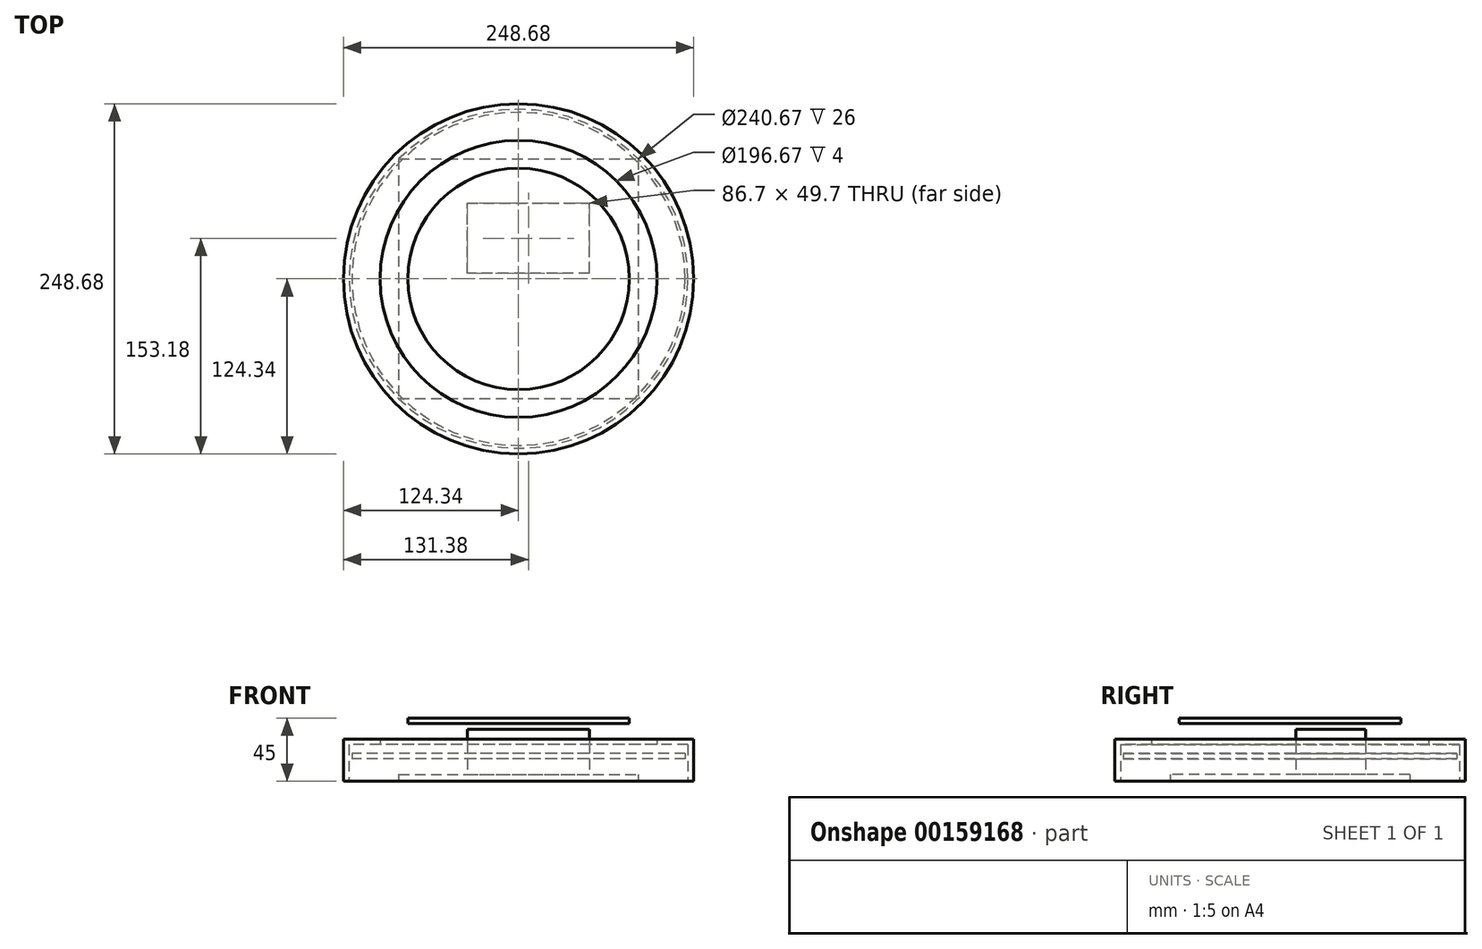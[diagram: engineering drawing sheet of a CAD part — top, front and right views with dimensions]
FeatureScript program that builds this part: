
annotation { "Feature Type Name" : "Feature", "Feature Type Description" : "" }
export const myFeature = defineFeature(function(context is Context, id is Id, definition is map)
    precondition{}
    {
        {
            var Q0;
            Q0=qCreatedBy(makeId("Top.planeOp"),FACE);
            var sketch = newSketch(context, id + "F0", { "sketchPlane" : qUnion([Q0])});
            skLineSegment(sketch, "E0.bottom", {"start": v(0, 0) * mm, "end": v(170.18, 0) * mm});
            skLineSegment(sketch, "E0.top", {"start": v(0, -170.18) * mm, "end": v(170.18, -170.18) * mm});
            skLineSegment(sketch, "E0.left", {"start": v(0, 0) * mm, "end": v(0, -170.18) * mm});
            skLineSegment(sketch, "E0.right", {"start": v(170.18, 0) * mm, "end": v(170.18, -170.18) * mm});
            skSolve(sketch);
        }
        {
            var Q0;
            Q0 = qSketchRegion(id + "F0", true);
            extrude(context, id + "F1", {"entities" : qUnion([Q0]), "depth" : 5 * mm});
        }
        {
            var Q0;
            Q0=makeQuery(id+"F1.opExtrude","CAP_FACE",FACE,{"disambiguationData":[OSD([sQuery(id+"F0.wireOp",EDGE,"E0.bottom"),sQuery(id+"F0.wireOp",EDGE,"E0.top"),sQuery(id+"F0.wireOp",EDGE,"E0.left"),sQuery(id+"F0.wireOp",EDGE,"E0.right")])],"isStart":true});
            var sketch = newSketch(context, id + "F2", { "sketchPlane" : qUnion([Q0])});
            skLineSegment(sketch, "E1.bottom", {"start": v(135.48, 81.1) * mm, "end": v(48.78, 81.1) * mm});
            skLineSegment(sketch, "E1.top", {"start": v(48.78, 31.4) * mm, "end": v(135.48, 31.4) * mm});
            skLineSegment(sketch, "E1.left", {"start": v(135.48, 81.1) * mm, "end": v(135.48, 31.4) * mm});
            skLineSegment(sketch, "E1.right", {"start": v(48.78, 81.1) * mm, "end": v(48.78, 31.4) * mm});
            skSolve(sketch);
        }
        {
            var Q0;
            Q0 = qSketchRegion(id + "F2", true);
            extrude(context, id + "F3", {"entities" : qUnion([Q0]), "operationType" : NewBodyOperationType.ADD, "oppositeDirection" : true, "depth" : 37 * mm});
        }
        {
            var Q0;
            Q0=qCreatedBy(makeId("Top.planeOp"),FACE);
            var sketch = newSketch(context, id + "F4", { "sketchPlane" : qUnion([Q0])});
            skCircle(sketch, "E2", {"center": v(85.1, -85.1) * mm, "radius": 120.34 * mm});
            skPoint(sketch, "E3", {"position": v(0, 0) * mm});
            skPoint(sketch, "E4", {"position": v(170.18, -170.18) * mm});
            skCircle(sketch, "E5", {"center": v(85.1, -85.1) * mm, "radius": 124.34 * mm});
            skSolve(sketch);
        }
        {
            var Q0;
            Q0=makeQuery(id+"F1.opExtrude","CAP_FACE",FACE,{"disambiguationData":[OSD([sQuery(id+"F0.wireOp",EDGE,"E0.bottom"),sQuery(id+"F0.wireOp",EDGE,"E0.top"),sQuery(id+"F0.wireOp",EDGE,"E0.left"),sQuery(id+"F0.wireOp",EDGE,"E0.right")])],"isStart":false});
            var sketch = newSketch(context, id + "F5", { "sketchPlane" : qUnion([Q0])});
            skCircle(sketch, "E6", {"center": v(85.1, -85.1) * mm, "radius": 118.34 * mm});
            skSolve(sketch);
        }
        {
            var Q0;
            Q0 = qSketchRegion(id + "F5", true);
            extrude(context, id + "F6", {"entities" : qUnion([Q0]), "operationType" : NewBodyOperationType.ADD, "depth" : (.4 * 37) * mm, "hasSecondDirection" : true, "secondDirectionOppositeDirection" : false, "secondDirectionDepth" : 11 * mm});
        }
        {
            var Q0;
            Q0=makeQuery(id+"F6.opExtrude","CAP_FACE",FACE,{"disambiguationData":[OSD([sQuery(id+"F5.wireOp",EDGE,"E6")])],"isStart":false});
            var sketch = newSketch(context, id + "F7", { "sketchPlane" : qUnion([Q0])});
            skCircle(sketch, "E7", {"center": v(85.1, -85.1) * mm, "radius": 108.34 * mm});
            skSolve(sketch);
        }
        {
            var Q0;
            Q0=makeQuery(id+"F4.imprint","IMPRINT",FACE,{"disambiguationData":[TD([[makeQuery(id+"F4.imprint","IMPRINT",EDGE,{"derivedFrom":sQuery(id+"F4.wireOp",EDGE,"E2")}),-1.0]])]});
            extrude(context, id + "F8", {"entities" : qUnion([Q0]), "depth" : 26 * mm});
        }
        {
            var Q0;
            Q0=makeQuery(id+"F8.opExtrude","CAP_FACE",FACE,{"disambiguationData":[OSD([sQuery(id+"F4.wireOp",EDGE,"E2"),sQuery(id+"F4.wireOp",EDGE,"E5")])],"isStart":false});
            var sketch = newSketch(context, id + "F9", { "sketchPlane" : qUnion([Q0])});
            skCircle(sketch, "E8", {"center": v(85.1, -85.1) * mm, "radius": 98.34 * mm});
            skCircle(sketch, "E9", {"center": v(85.1, -85.1) * mm, "radius": 124.34 * mm});
            skSolve(sketch);
        }
        {
            var Q0;
            Q0 = qSketchRegion(id + "F9", true);
            extrude(context, id + "F10", {"entities" : qUnion([Q0]), "operationType" : NewBodyOperationType.ADD, "depth" : 4 * mm});
        }
        {
            var Q0;
            Q0=makeQuery(id+"F3.opExtrude","CAP_FACE",FACE,{"disambiguationData":[OSD([sQuery(id+"F2.wireOp",EDGE,"E1.bottom"),sQuery(id+"F2.wireOp",EDGE,"E1.top"),sQuery(id+"F2.wireOp",EDGE,"E1.left"),sQuery(id+"F2.wireOp",EDGE,"E1.right")])],"isStart":false});
            var sketch = newSketch(context, id + "F11", { "sketchPlane" : qUnion([Q0])});
            skCircle(sketch, "E10", {"center": v(85.1, -85.1) * mm, "radius": 78.62 * mm});
            skSolve(sketch);
        }
        {
            var Q0;
            Q0 = qSketchRegion(id + "F11", true);
            extrude(context, id + "F12", {"entities" : qUnion([Q0]), "depth" : 8 * mm, "hasSecondDirection" : true, "secondDirectionOppositeDirection" : false, "secondDirectionDepth" : 4 * mm});
        }
        {
            var Q0;
            Q0=makeQuery(id+"F10.opExtrude","SWEPT_FACE",FACE,{"disambiguationData":[OSD([sQuery(id+"F9.wireOp",EDGE,"E8")])]});
            var Q1;
            Q1=makeQuery(id+"F12.opExtrude","SWEPT_FACE",FACE,{"disambiguationData":[OSD([sQuery(id+"F11.wireOp",EDGE,"E10")])]});
            var Q2;
            Q2=makeQuery(id+"F12.opExtrude","CAP_EDGE",EDGE,{"disambiguationData":[OSD([sQuery(id+"F11.wireOp",EDGE,"E10")])],"isStart":false});
            var Q3;
            Q3=makeQuery(id+"F10.opExtrude","CAP_EDGE",EDGE,{"disambiguationData":[OSD([sQuery(id+"F9.wireOp",EDGE,"E8")])],"isStart":false});
            loft(context, id + "F13", {"bodyType" : ToolBodyType.SURFACE, "sheetProfilesArray" : [{ "sheetProfileEntities" : qUnion([Q0]) }, { "sheetProfileEntities" : qUnion([Q1]) }], "wireProfilesArray" : [{ "wireProfileEntities" : qUnion([Q2]) }, { "wireProfileEntities" : qUnion([Q3]) }]});
        }
    });
